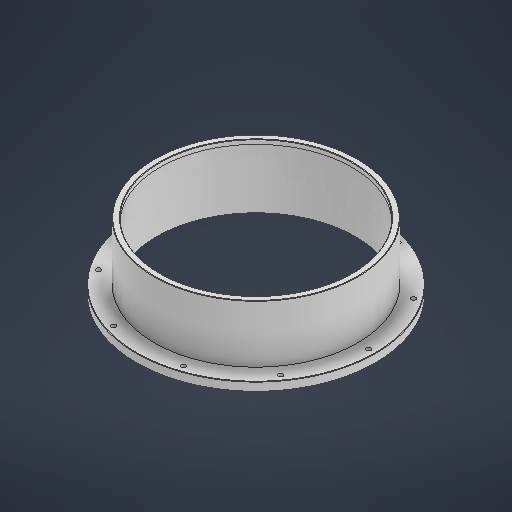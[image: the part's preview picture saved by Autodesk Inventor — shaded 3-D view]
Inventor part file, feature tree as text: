
AUTODESK INVENTOR PART (.ipt)
format: ipt  version: 2025 (Build 290162000, 162)  size: 299,008 bytes
history: native  units: in
note: dims shown in document units (in); Inventor stores cm internally (conversion verified against a paired STEP export)
features: other x12, sketch x6, extrude x4, chamfer x2, hole x1
ambient origin geometry x8: Origin, YZ Plane, XZ Plane, XY Plane, X Axis, Y Axis, Z Axis, Center Point
bodies: Solid1 (feature_tree)
feature tree (25):
  other  "Table"
  other  "Cylinder Segment - 01"
  other  "Cylinder Segment - 02"
  other  "Cylinder Segment - 03"
  other  "Cylinder Segment - 04"
  other  "Cylinder Segment - 05"
  other  "Cylinder Segment - 06"
  other  "Cylinder Segment - 07"
  other  "Cylinder Segment - 08"
  other  "Cylinder Segment - 09"
  other  "Cylinder Segment - 10"
  other  "Cylinder Segment - Face"
  sketch  "Sketch1"  dims[d5=0.0in d7=0.0in]
  extrude  "Extrusion1"  TaperAngle=0.0deg  [1 undecoded]
  extrude  "Extrusion2"  Depth=0.0787in TaperAngle=45.0deg
  extrude  "Extrusion7"  Depth=10.0394in
  chamfer  "Chamfer1"  Distance=3.937in Angle=360.0deg
  chamfer  "Chamfer2"  Distance=0.3937in
  extrude  "Extrusion8"  Depth=0.0787in
  hole  "Hole1"  [1 undecoded]
  sketch  "Sketch2"  dims[d25=0.0787in d26=45.0deg d27=10.0394in]
  sketch  "Sketch3"  dims[d35=3.1496in d36=0.0787in]
  sketch  "Sketch Circular Pattern1"  dims[d18=0.0in d22=0.0787in d23=45.0deg]
  sketch  "Sketch4"  dims[d37=2.7559in d39=360.0deg d41=0.0617in d42=0.1575in d43=0.1575in d44=0.0787in d45=90.0deg d46=0.248in d47=0.8108in]
  sketch  "Sketch Circular Pattern2"  dims[d28=0.1969in d29=3.937in d31=360.0deg d33=0.3937in d34=0.0in]
note: 2 required parameter values undecoded (feature->parameter linkage not recoverable at this tier; creation-order binding heuristic only, values carry confidence <= 0.55)
